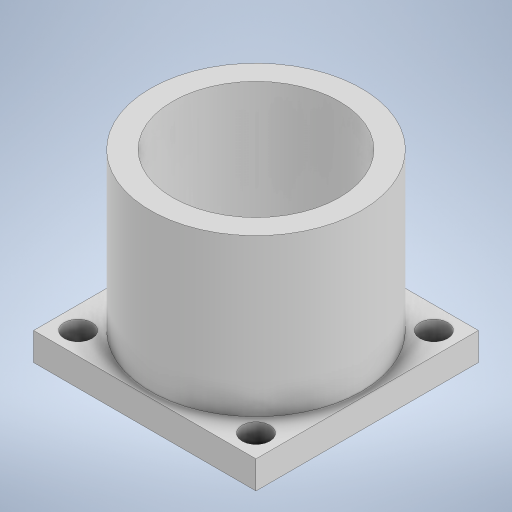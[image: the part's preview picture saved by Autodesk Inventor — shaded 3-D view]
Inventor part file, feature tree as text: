
AUTODESK INVENTOR PART (.ipt)
format: ipt  version: 2023 (Build 270158000, 158)  size: 235,008 bytes
history: native  units: in
note: dims shown in document units (in); Inventor stores cm internally (conversion verified against a paired STEP export)
features: extrude x3, sketch x1
ambient origin geometry x8: Origin, YZ Plane, XZ Plane, XY Plane, X Axis, Y Axis, Z Axis, Center Point
bodies: Solid1 (feature_tree)
feature tree (4):
  sketch  "Sketch1"  dims[d6=1.66in d7=0.0in d10=2.0in d11=2.0in d12=0.25in d13=0.0in d20=0.25in d23=0.25in d24=0.0in]
  extrude  "Extrusion1"  Depth=2.0in
  extrude  "Extrusion3"  Depth=2.0in
  extrude  "Extrusion5"  Depth=0.25in TaperAngle=0.0deg
